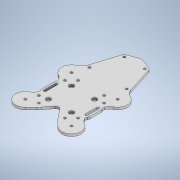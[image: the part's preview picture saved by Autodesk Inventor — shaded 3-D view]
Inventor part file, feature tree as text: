
AUTODESK INVENTOR PART (.ipt)
format: ipt  version: 2020 (Build 240168000, 168)  size: 273,408 bytes
history: native  units: in
note: dims shown in document units (in); Inventor stores cm internally (conversion verified against a paired STEP export)
features: extrude x2, sketch x2, projected_geometry x1
ambient origin geometry x8: Origin, YZ Plane, XZ Plane, XY Plane, X Axis, Y Axis, Z Axis, Center Point
bodies: Solid1 (feature_tree)
feature tree (5):
  extrude  "Extrusion1"  Depth=0.3937in
  extrude  "Extrusion2"  Depth=0.1181in
  sketch  "Sketch1"  dims[d0=0.1181in d1=0.0in d2=0.3937in]
  sketch  "Sketch2"  dims[d3=0.3937in d4=0.5906in d5=0.5906in d6=0.1181in d7=0.0in d8=0.122in d9=0.122in d10=0.122in]
  projected_geometry  "Projected Loop1"
